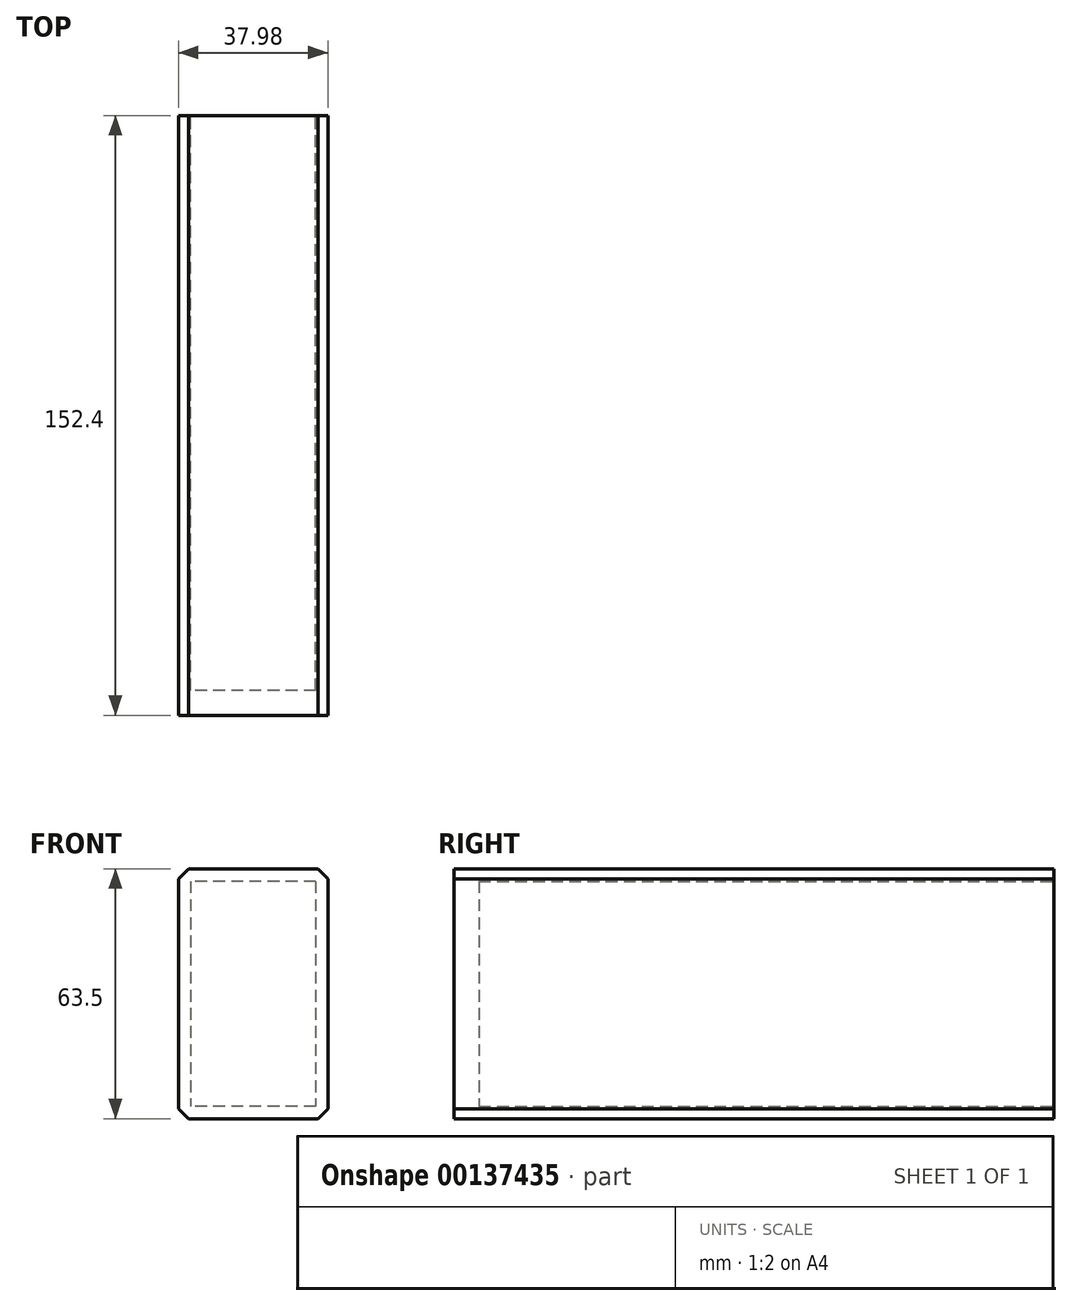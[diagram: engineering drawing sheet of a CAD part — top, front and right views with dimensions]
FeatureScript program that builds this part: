
annotation { "Feature Type Name" : "Feature", "Feature Type Description" : "" }
export const myFeature = defineFeature(function(context is Context, id is Id, definition is map)
    precondition{}
    {
        {
            var Q0;
            Q0=qCreatedBy(makeId("Front.planeOp"),FACE);
            var sketch = newSketch(context, id + "F0", { "sketchPlane" : qUnion([Q0])});
            skLineSegment(sketch, "E0.bottom", {"start": v(18.99, 31.75) * mm, "end": v(-18.99, 31.75) * mm});
            skLineSegment(sketch, "E0.top", {"start": v(18.99, -31.75) * mm, "end": v(-18.99, -31.75) * mm});
            skLineSegment(sketch, "E0.left", {"start": v(18.99, 31.75) * mm, "end": v(18.99, -31.75) * mm});
            skLineSegment(sketch, "E0.right", {"start": v(-18.99, 31.75) * mm, "end": v(-18.99, -31.75) * mm});
            skPoint(sketch, "E0.middle", {"position": v(0, 0) * mm});
            skLineSegment(sketch, "E1.bottom", {"start": v(15.86, 28.58) * mm, "end": v(-15.86, 28.58) * mm});
            skLineSegment(sketch, "E1.top", {"start": v(15.86, -28.58) * mm, "end": v(-15.86, -28.58) * mm});
            skLineSegment(sketch, "E1.left", {"start": v(15.86, 28.58) * mm, "end": v(15.86, -28.58) * mm});
            skLineSegment(sketch, "E1.right", {"start": v(-15.86, 28.58) * mm, "end": v(-15.86, -28.58) * mm});
            skSolve(sketch);
        }
        {
            var Q0;
            Q0=makeQuery(id+"F0.imprint","IMPRINT",FACE,{"disambiguationData":[TD([[makeQuery(id+"F0.imprint","IMPRINT",EDGE,{"derivedFrom":sQuery(id+"F0.wireOp",EDGE,"E0.bottom")}),1.0]])]});
            extrude(context, id + "F1", {"entities" : qUnion([Q0]), "depth" : 152.4 * mm});
        }
        {
            var Q0;
            Q0=makeQuery(id+"F1.opExtrude","CAP_FACE",FACE,{"disambiguationData":[OSD([sQuery(id+"F0.wireOp",EDGE,"E0.bottom"),sQuery(id+"F0.wireOp",EDGE,"E0.top"),sQuery(id+"F0.wireOp",EDGE,"E0.left"),sQuery(id+"F0.wireOp",EDGE,"E0.right"),sQuery(id+"F0.wireOp",EDGE,"E1.bottom"),sQuery(id+"F0.wireOp",EDGE,"E1.top"),sQuery(id+"F0.wireOp",EDGE,"E1.left"),sQuery(id+"F0.wireOp",EDGE,"E1.right")])],"isStart":false});
            var sketch = newSketch(context, id + "F2", { "sketchPlane" : qUnion([Q0])});
            skLineSegment(sketch, "E2.bottom", {"start": v(-18.99, 31.75) * mm, "end": v(18.99, 31.75) * mm});
            skLineSegment(sketch, "E2.top", {"start": v(-18.99, -31.75) * mm, "end": v(18.99, -31.75) * mm});
            skLineSegment(sketch, "E2.left", {"start": v(-18.99, 31.75) * mm, "end": v(-18.99, -31.75) * mm});
            skLineSegment(sketch, "E2.right", {"start": v(18.99, 31.75) * mm, "end": v(18.99, -31.75) * mm});
            skSolve(sketch);
        }
        {
            var Q0;
            Q0 = qSketchRegion(id + "F2", true);
            extrude(context, id + "F3", {"entities" : qUnion([Q0]), "operationType" : NewBodyOperationType.ADD, "oppositeDirection" : true, "depth" : 6.35 * mm});
        }
        {
            var Q0;
            Q0=makeQuery(id+"F1.opExtrude","CAP_FACE",FACE,{"disambiguationData":[OSD([sQuery(id+"F0.wireOp",EDGE,"E0.bottom"),sQuery(id+"F0.wireOp",EDGE,"E0.top"),sQuery(id+"F0.wireOp",EDGE,"E0.left"),sQuery(id+"F0.wireOp",EDGE,"E0.right"),sQuery(id+"F0.wireOp",EDGE,"E1.bottom"),sQuery(id+"F0.wireOp",EDGE,"E1.top"),sQuery(id+"F0.wireOp",EDGE,"E1.left"),sQuery(id+"F0.wireOp",EDGE,"E1.right")])],"isStart":true});
            var sketch = newSketch(context, id + "F4", { "sketchPlane" : qUnion([Q0])});
            skLineSegment(sketch, "E3.bottom", {"start": v(15.86, 0) * mm, "end": v(18.99, 0) * mm});
            skLineSegment(sketch, "E3.top", {"start": v(15.86, 12.7) * mm, "end": v(18.99, 12.7) * mm});
            skLineSegment(sketch, "E3.left", {"start": v(15.86, 0) * mm, "end": v(15.86, 12.7) * mm});
            skLineSegment(sketch, "E3.right", {"start": v(18.99, 0) * mm, "end": v(18.99, 12.7) * mm});
            skLineSegment(sketch, "E4.top", {"start": v(15.86, -12.7) * mm, "end": v(18.99, -12.7) * mm});
            skLineSegment(sketch, "E4.left", {"start": v(15.86, 0) * mm, "end": v(15.86, -12.7) * mm});
            skLineSegment(sketch, "E4.right", {"start": v(18.99, 0) * mm, "end": v(18.99, -12.7) * mm});
            skSolve(sketch);
        }
        {
            var Q0;
            Q0=makeQuery(id+"F1.opExtrude","SWEPT_EDGE",EDGE,{"disambiguationData":[OSD([sQuery(id+"F0.wireOp",EDGE,"E0.bottom"),sQuery(id+"F0.wireOp",EDGE,"E0.left")])]});
            var Q1;
            Q1=makeQuery(id+"F1.opExtrude","SWEPT_EDGE",EDGE,{"disambiguationData":[OSD([sQuery(id+"F0.wireOp",EDGE,"E0.bottom"),sQuery(id+"F0.wireOp",EDGE,"E0.right")])]});
            var Q2;
            Q2=makeQuery(id+"F1.opExtrude","SWEPT_EDGE",EDGE,{"disambiguationData":[OSD([sQuery(id+"F0.wireOp",EDGE,"E0.top"),sQuery(id+"F0.wireOp",EDGE,"E0.left")])]});
            var Q3;
            Q3=makeQuery(id+"F1.opExtrude","SWEPT_EDGE",EDGE,{"disambiguationData":[OSD([sQuery(id+"F0.wireOp",EDGE,"E0.top"),sQuery(id+"F0.wireOp",EDGE,"E0.right")])]});
            chamfer(context, id + "F5", {"entities" : qUnion([Q0, Q1, Q2, Q3]), "width" : 2.54 * mm, "tangentPropagation" : true});
        }
    });
